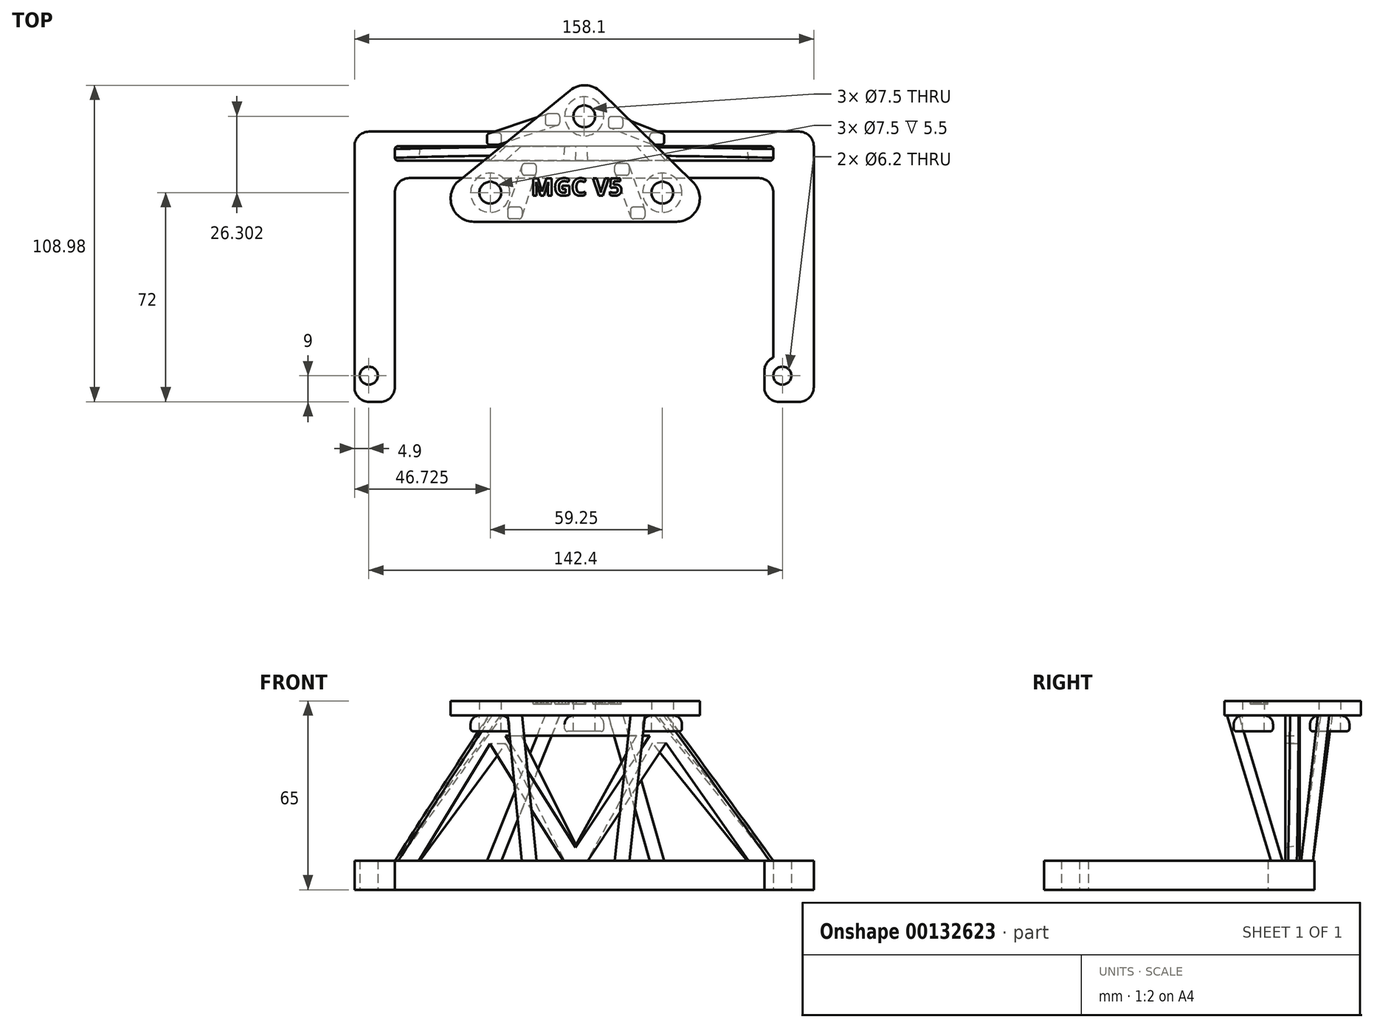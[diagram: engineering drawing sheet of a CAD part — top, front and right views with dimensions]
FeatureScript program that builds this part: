
annotation { "Feature Type Name" : "Feature", "Feature Type Description" : "" }
export const myFeature = defineFeature(function(context is Context, id is Id, definition is map)
    precondition{}
    {
        {
            var Q0;
            Q0=qCreatedBy(makeId("Top.planeOp"),FACE);
            var sketch = newSketch(context, id + "F0", { "sketchPlane" : qUnion([Q0])});
            skCircle(sketch, "E0", {"center": v(71.2, -68) * mm, "radius": 3.1 * mm});
            skCircle(sketch, "E1", {"center": v(-71.2, -68) * mm, "radius": 3.1 * mm});
            skLineSegment(sketch, "E2.bottom", {"start": v(68.1, -61.8) * mm, "end": v(82, -61.8) * mm});
            skLineSegment(sketch, "E2.top", {"start": v(68.1, 0) * mm, "end": v(82, 0) * mm});
            skLineSegment(sketch, "E2.left", {"start": v(68.1, -61.8) * mm, "end": v(68.1, 0) * mm});
            skLineSegment(sketch, "E2.right", {"start": v(82, -61.8) * mm, "end": v(82, 0) * mm});
            skLineSegment(sketch, "E3.bottom", {"start": v(82, -61.8) * mm, "end": v(65, -61.8) * mm});
            skLineSegment(sketch, "E3.top", {"start": v(82, -77) * mm, "end": v(65, -77) * mm});
            skLineSegment(sketch, "E3.left", {"start": v(82, -61.8) * mm, "end": v(82, -77) * mm});
            skLineSegment(sketch, "E3.right", {"start": v(65, -61.8) * mm, "end": v(65, -77) * mm});
            skLineSegment(sketch, "E4.bottom", {"start": v(-76.1, -77) * mm, "end": v(-62.2, -77) * mm});
            skLineSegment(sketch, "E4.top", {"start": v(-76.1, 0) * mm, "end": v(-62.2, 0) * mm});
            skLineSegment(sketch, "E4.left", {"start": v(-76.1, -77) * mm, "end": v(-76.1, 0) * mm});
            skLineSegment(sketch, "E4.right", {"start": v(-62.2, -77) * mm, "end": v(-62.2, 0) * mm});
            skLineSegment(sketch, "E5.bottom", {"start": v(-76.1, 0) * mm, "end": v(82, 0) * mm});
            skLineSegment(sketch, "E5.top", {"start": v(-76.1, 16) * mm, "end": v(82, 16) * mm});
            skLineSegment(sketch, "E5.left", {"start": v(-76.1, 0) * mm, "end": v(-76.1, 16) * mm});
            skLineSegment(sketch, "E5.right", {"start": v(82, 0) * mm, "end": v(82, 16) * mm});
            skPoint(sketch, "E6", {"position": v(68.1, -68) * mm});
            skSolve(sketch);
        }
        {
            var Q0;
            Q0=makeQuery(id+"F0.imprint","IMPRINT",FACE,{"disambiguationData":[TD([[makeQuery(id+"F0.imprint","IMPRINT",EDGE,{"derivedFrom":sQuery(id+"F0.wireOp",EDGE,"E1")}),-1.0]])]});
            var Q1;
            Q1=makeQuery(id+"F0.imprint","IMPRINT",FACE,{"disambiguationData":[TD([[makeQuery(id+"F0.imprint","IMPRINT",EDGE,{"derivedFrom":sQuery(id+"F0.wireOp",EDGE,"E0")}),-1.0]])]});
            var Q2;
            {var subQ0=sQuery(id+"F0.wireOp",EDGE,"E2.left");Q2=makeQuery(id+"F0.imprint","IMPRINT",FACE,{"disambiguationData":[TD([[makeQuery(id+"F0.imprint","IMPRINT",EDGE,{"derivedFrom":subQ0}),-1.0]])]});}
            var Q3;
            Q3=makeQuery(id+"F0.imprint","IMPRINT",FACE,{"disambiguationData":[TD([[makeQuery(id+"F0.imprint","IMPRINT",EDGE,{"derivedFrom":sQuery(id+"F0.wireOp",EDGE,"E5.top")}),-1.0]])]});
            extrude(context, id + "F1", {"entities" : qUnion([Q0, Q1, Q2, Q3]), "depth" : 10 * mm, "symmetric" : true});
        }
        {
            var Q0;
            Q0=qCreatedBy(makeId("Top.planeOp"),FACE);
            cPlane(context, id + "F2", {"entities" : qUnion([Q0]), "cplaneType" : CPlaneType.OFFSET, "offset" : 55 * mm, "width" : 150 * mm, "height" : 150 * mm});
        }
        {
            var Q0;
            Q0=qCreatedBy(id+"F2.planeOp",FACE);
            var sketch = newSketch(context, id + "F3", { "sketchPlane" : qUnion([Q0])});
            skCircle(sketch, "E7", {"center": v(-29.38, -5) * mm, "radius": 3.75 * mm});
            skCircle(sketch, "E8", {"center": v(29.88, -5) * mm, "radius": 3.75 * mm});
            skCircle(sketch, "E9", {"center": v(3, 21.3) * mm, "radius": 3.75 * mm});
            skLineSegment(sketch, "E10", {"start": v(-29.38, -5) * mm, "end": v(3, 21.3) * mm});
            skLineSegment(sketch, "E11", {"start": v(3, 21.3) * mm, "end": v(29.88, -5) * mm});
            skLineSegment(sketch, "E12", {"start": v(29.88, -5) * mm, "end": v(-29.38, -5) * mm});
            skLineSegment(sketch, "E13.0", {"start": v(-40.05, -0.8) * mm, "end": v(-1.92, 30.19) * mm});
            skLineSegment(sketch, "E13.1", {"start": v(34.78, -15) * mm, "end": v(-35, -15) * mm});
            skLineSegment(sketch, "E13.2", {"start": v(8.72, 29.7) * mm, "end": v(40.37, -1.28) * mm});
            skPoint(sketch, "E14.visualSharp", {"position": v(3.62, 34.69) * mm});
            skArc(sketch, "E14.filletArc", {"start": v(8.72, 29.7) * mm, "mid": v(3.49, 31.97) * mm, "end": v(-1.92, 30.19) * mm});
            skPoint(sketch, "E15.visualSharp", {"position": v(-57.54, -15) * mm});
            skArc(sketch, "E15.filletArc", {"start": v(-40.05, -0.8) * mm, "mid": v(-42.55, -9.68) * mm, "end": v(-35, -15) * mm});
            skPoint(sketch, "E16.visualSharp", {"position": v(54.4, -15) * mm});
            skArc(sketch, "E16.filletArc", {"start": v(34.78, -15) * mm, "mid": v(42.19, -10.02) * mm, "end": v(40.37, -1.28) * mm});
            skPoint(sketch, "E17", {"position": v(-0.11, -15) * mm});
            skCircle(sketch, "E18", {"center": v(-0.11, -10) * mm, "radius": 2.5 * mm});
            skSolve(sketch);
        }
        {
            var Q0;
            Q0=makeQuery(id+"F3.imprint","IMPRINT",FACE,{"disambiguationData":[TD([[makeQuery(id+"F3.imprint","IMPRINT",EDGE,{"derivedFrom":sQuery(id+"F3.wireOp",EDGE,"E13.0")}),-1.0]])]});
            var Q1;
            {var subQ0=sQuery(id+"F3.wireOp",EDGE,"E10");var subQ1=sQuery(id+"F3.wireOp",EDGE,"E7");var subQ2=makeQuery(id+"F3.imprint","INTERSECT",VERTEX,{"derivedFrom":[subQ1,subQ0]});Q1=makeQuery(id+"F3.imprint","IMPRINT",FACE,{"disambiguationData":[TD([[makeQuery(id+"F3.imprint","IMPRINT",EDGE,{"disambiguationData":[TD([[subQ2,1.0]])],"derivedFrom":subQ1}),-1.0]])]});}
            var Q2;
            Q2=makeQuery(id+"F3.imprint","IMPRINT",FACE,{"disambiguationData":[TD([[makeQuery(id+"F3.imprint","IMPRINT",EDGE,{"derivedFrom":sQuery(id+"F3.wireOp",EDGE,"E18")}),1.0]])]});
            extrude(context, id + "F4", {"entities" : qUnion([Q0, Q1, Q2]), "depth" : 5 * mm});
        }
        {
            var Q0;
            Q0=makeQuery(id+"F1.opExtrude","SWEPT_FACE",FACE,{"disambiguationData":[OSD([sQuery(id+"F0.wireOp",EDGE,"E5.bottom")])]});
            cPlane(context, id + "F5", {"entities" : qUnion([Q0]), "cplaneType" : CPlaneType.OFFSET, "offset" : 6 * mm, "oppositeDirection" : true, "width" : 150 * mm, "height" : 150 * mm});
        }
        {
            var Q0;
            Q0=qCreatedBy(id+"F5.planeOp",FACE);
            var sketch = newSketch(context, id + "F6", { "sketchPlane" : qUnion([Q0])});
            skLineSegment(sketch, "E19", {"start": v(32.93, 55) * mm, "end": v(-31.7, 55) * mm});
            skLineSegment(sketch, "E20", {"start": v(-31.7, 55) * mm, "end": v(-62.2, 5) * mm});
            skLineSegment(sketch, "E21", {"start": v(-62.2, 5) * mm, "end": v(68.1, 5) * mm});
            skLineSegment(sketch, "E22", {"start": v(68.1, 5) * mm, "end": v(32.93, 55) * mm});
            skSolve(sketch);
        }
        {
            var Q0;
            Q0=makeQuery(id+"F6.imprint","IMPRINT",FACE,{"disambiguationData":[TD([[makeQuery(id+"F6.imprint","IMPRINT",EDGE,{"derivedFrom":sQuery(id+"F6.wireOp",EDGE,"E19")}),1.0]])]});
            cPlane(context, id + "F7", {"entities" : qUnion([Q0]), "cplaneType" : CPlaneType.OFFSET, "offset" : 5 * mm, "oppositeDirection" : true, "width" : 150 * mm, "height" : 150 * mm});
        }
        {
            var Q0;
            Q0=qCreatedBy(id+"F7.planeOp",FACE);
            var sketch = newSketch(context, id + "F8", { "sketchPlane" : qUnion([Q0])});
            skLineSegment(sketch, "E23", {"start": v(27.82, 55) * mm, "end": v(-25.54, 55) * mm});
            skLineSegment(sketch, "E24", {"start": v(68.1, 5) * mm, "end": v(-62.2, 5) * mm});
            skPoint(sketch, "E25.0", {"position": v(68.1, 5) * mm});
            skPoint(sketch, "E26.0", {"position": v(-62.2, 5) * mm});
            skLineSegment(sketch, "E27", {"start": v(27.82, 55) * mm, "end": v(68.1, 5) * mm});
            skLineSegment(sketch, "E28", {"start": v(-25.54, 55) * mm, "end": v(-62.2, 5) * mm});
            skSolve(sketch);
        }
        {
            var Q0;
            Q0=makeQuery(id+"F6.imprint","IMPRINT",FACE,{"disambiguationData":[TD([[makeQuery(id+"F6.imprint","IMPRINT",EDGE,{"derivedFrom":sQuery(id+"F6.wireOp",EDGE,"E19")}),1.0]])]});
            var Q1;
            Q1=makeQuery(id+"F8.imprint","IMPRINT",FACE,{"disambiguationData":[TD([[makeQuery(id+"F8.imprint","IMPRINT",EDGE,{"derivedFrom":sQuery(id+"F8.wireOp",EDGE,"E23")}),1.0]])]});
            loft(context, id + "F9", {"sheetProfilesArray" : [{ "sheetProfileEntities" : qUnion([Q0]) }, { "sheetProfileEntities" : qUnion([Q1]) }]});
        }
        {
            var Q0;
            Q0=makeQuery(id+"F1.opExtrude","SWEPT_EDGE",EDGE,{"disambiguationData":[OSD([sQuery(id+"F0.wireOp",EDGE,"E5.top"),sQuery(id+"F0.wireOp",EDGE,"E5.right")])]});
            var Q1;
            Q1=makeQuery(id+"F1.opExtrude","SWEPT_EDGE",EDGE,{"disambiguationData":[OSD([sQuery(id+"F0.wireOp",EDGE,"E5.top"),sQuery(id+"F0.wireOp",EDGE,"E5.left")])]});
            var Q2;
            Q2=makeQuery(id+"F1.opExtrude","SWEPT_EDGE",EDGE,{"disambiguationData":[OSD([sQuery(id+"F0.wireOp",EDGE,"E4.bottom"),sQuery(id+"F0.wireOp",EDGE,"E4.left")])]});
            var Q3;
            Q3=makeQuery(id+"F1.opExtrude","SWEPT_EDGE",EDGE,{"disambiguationData":[OSD([sQuery(id+"F0.wireOp",EDGE,"E4.bottom"),sQuery(id+"F0.wireOp",EDGE,"E4.right")])]});
            var Q4;
            Q4=makeQuery(id+"F1.opExtrude","SWEPT_EDGE",EDGE,{"disambiguationData":[OSD([sQuery(id+"F0.wireOp",EDGE,"E3.bottom"),sQuery(id+"F0.wireOp",EDGE,"E3.right")])]});
            var Q5;
            Q5=makeQuery(id+"F1.opExtrude","SWEPT_EDGE",EDGE,{"disambiguationData":[OSD([sQuery(id+"F0.wireOp",EDGE,"E3.top"),sQuery(id+"F0.wireOp",EDGE,"E3.right")])]});
            var Q6;
            Q6=makeQuery(id+"F1.opExtrude","SWEPT_EDGE",EDGE,{"disambiguationData":[OSD([sQuery(id+"F0.wireOp",EDGE,"E3.top"),sQuery(id+"F0.wireOp",EDGE,"E3.left")])]});
            var Q7;
            Q7=makeQuery(id+"F1.opExtrude","SWEPT_EDGE",EDGE,{"disambiguationData":[OSD([sQuery(id+"F0.wireOp",EDGE,"E4.right"),sQuery(id+"F0.wireOp",EDGE,"E5.bottom")])]});
            var Q8;
            Q8=makeQuery(id+"F1.opExtrude","SWEPT_EDGE",EDGE,{"disambiguationData":[OSD([sQuery(id+"F0.wireOp",EDGE,"E2.left"),sQuery(id+"F0.wireOp",EDGE,"E5.bottom")])]});
            var Q9;
            Q9=makeQuery(id+"FIhUJoxLiTrV3G5_2.opExtrude","SWEPT_EDGE",EDGE,{"disambiguationData":[OSD([sQuery(id+"F6.wireOp",EDGE,"E19"),sQuery(id+"F6.wireOp",EDGE,"E22")])]});
            var Q10;
            Q10=makeQuery(id+"FIhUJoxLiTrV3G5_2.opExtrude","SWEPT_EDGE",EDGE,{"disambiguationData":[OSD([sQuery(id+"F6.wireOp",EDGE,"E19"),sQuery(id+"F6.wireOp",EDGE,"E20")])]});
            fillet(context, id + "F10", {"entities" : qUnion([Q0, Q1, Q2, Q3, Q4, Q5, Q6, Q7, Q8, Q9, Q10]), "radius" : 5 * mm, "tangentPropagation" : true, "allowEdgeOverflow" : false});
        }
        {
            var Q0;
            Q0=makeQuery(id+"F4.opExtrude","CAP_FACE",FACE,{"disambiguationData":[OSD([sQuery(id+"F3.wireOp",EDGE,"E7"),sQuery(id+"F3.wireOp",EDGE,"E8"),sQuery(id+"F3.wireOp",EDGE,"E9"),sQuery(id+"F3.wireOp",EDGE,"E13.0"),sQuery(id+"F3.wireOp",EDGE,"E13.1"),sQuery(id+"F3.wireOp",EDGE,"E13.2"),sQuery(id+"F3.wireOp",EDGE,"E14.filletArc"),sQuery(id+"F3.wireOp",EDGE,"E15.filletArc"),sQuery(id+"F3.wireOp",EDGE,"E16.filletArc")])],"isStart":false});
            var sketch = newSketch(context, id + "F11", { "sketchPlane" : qUnion([Q0])});
            skText(sketch, "E29", { "text": "MGC V5", "fontName": "OpenSans-Bold.ttf"});
            const initialGuessF11  = {"E29": [-0.01538, -0.006, 1, 0, 0.006]};
            skSetInitialGuess(sketch, initialGuessF11);
            skSolve(sketch);
        }
        {
            var Q0;
            Q0 = qSketchRegion(id + "F11", true);
            extrude(context, id + "F12", {"entities" : qUnion([Q0]), "operationType" : NewBodyOperationType.REMOVE, "oppositeDirection" : true, "depth" : 1 * mm});
        }
        {
            var Q0;
            Q0=makeQuery(id+"F4.opExtrude","SWEPT_BODY",BODY,{"disambiguationData":[OSD([sQuery(id+"F3.wireOp",EDGE,"E7"),sQuery(id+"F3.wireOp",EDGE,"E8"),sQuery(id+"F3.wireOp",EDGE,"E9"),sQuery(id+"F3.wireOp",EDGE,"E13.0"),sQuery(id+"F3.wireOp",EDGE,"E13.1"),sQuery(id+"F3.wireOp",EDGE,"E13.2"),sQuery(id+"F3.wireOp",EDGE,"E14.filletArc"),sQuery(id+"F3.wireOp",EDGE,"E15.filletArc"),sQuery(id+"F3.wireOp",EDGE,"E16.filletArc")])]});
            var Q1;
            Q1=makeQuery(id+"F1.opExtrude","SWEPT_BODY",BODY,{"disambiguationData":[OSD([sQuery(id+"F0.wireOp",EDGE,"E0"),sQuery(id+"F0.wireOp",EDGE,"E1"),sQuery(id+"F0.wireOp",EDGE,"E2.left"),sQuery(id+"F0.wireOp",EDGE,"E2.right"),sQuery(id+"F0.wireOp",EDGE,"E3.bottom"),sQuery(id+"F0.wireOp",EDGE,"E3.top"),sQuery(id+"F0.wireOp",EDGE,"E3.left"),sQuery(id+"F0.wireOp",EDGE,"E3.right"),sQuery(id+"F0.wireOp",EDGE,"E4.bottom"),sQuery(id+"F0.wireOp",EDGE,"E4.left"),sQuery(id+"F0.wireOp",EDGE,"E4.right"),sQuery(id+"F0.wireOp",EDGE,"E5.bottom"),sQuery(id+"F0.wireOp",EDGE,"E5.top"),sQuery(id+"F0.wireOp",EDGE,"E5.left"),sQuery(id+"F0.wireOp",EDGE,"E5.right")])]});
            var Q2;
            Q2=makeQuery(id+"F9.opLoft","SWEPT_BODY",BODY,{"disambiguationData":[OSD([makeQuery(id+"F6.imprint","IMPRINT",FACE,{"disambiguationData":[TD([[makeQuery(id+"F6.imprint","IMPRINT",EDGE,{"derivedFrom":sQuery(id+"F6.wireOp",EDGE,"E19")}),1.0]])]}),makeQuery(id+"F8.imprint","IMPRINT",FACE,{"disambiguationData":[TD([[makeQuery(id+"F8.imprint","IMPRINT",EDGE,{"derivedFrom":sQuery(id+"F8.wireOp",EDGE,"E23")}),1.0]])]})])]});
            booleanBodies(context, id + "F13", {"operationType" : BooleanOperationType.UNION, "tools" : qUnion([Q0, Q1, Q2])});
        }
        {
            var Q0;
            Q0=makeQuery(id+"F1.opExtrude","CAP_FACE",FACE,{"disambiguationData":[OSD([sQuery(id+"F0.wireOp",EDGE,"E0"),sQuery(id+"F0.wireOp",EDGE,"E1"),sQuery(id+"F0.wireOp",EDGE,"E2.left"),sQuery(id+"F0.wireOp",EDGE,"E2.right"),sQuery(id+"F0.wireOp",EDGE,"E3.bottom"),sQuery(id+"F0.wireOp",EDGE,"E3.top"),sQuery(id+"F0.wireOp",EDGE,"E3.left"),sQuery(id+"F0.wireOp",EDGE,"E3.right"),sQuery(id+"F0.wireOp",EDGE,"E4.bottom"),sQuery(id+"F0.wireOp",EDGE,"E4.left"),sQuery(id+"F0.wireOp",EDGE,"E4.right"),sQuery(id+"F0.wireOp",EDGE,"E5.bottom"),sQuery(id+"F0.wireOp",EDGE,"E5.top"),sQuery(id+"F0.wireOp",EDGE,"E5.left"),sQuery(id+"F0.wireOp",EDGE,"E5.right")])],"isStart":false});
            var sketch = newSketch(context, id + "F14", { "sketchPlane" : qUnion([Q0])});
            skLineSegment(sketch, "E30.bottom", {"start": v(-13.5, 1) * mm, "end": v(-18.5, 1) * mm});
            skLineSegment(sketch, "E30.top", {"start": v(-13.5, 5) * mm, "end": v(-18.5, 5) * mm});
            skLineSegment(sketch, "E30.left", {"start": v(-13.5, 1) * mm, "end": v(-13.5, 5) * mm});
            skLineSegment(sketch, "E30.right", {"start": v(-18.5, 1) * mm, "end": v(-18.5, 5) * mm});
            skPoint(sketch, "E30.middle", {"position": v(-16, 3) * mm});
            skLineSegment(sketch, "E31.bottom", {"start": v(18.5, 1) * mm, "end": v(13.5, 1) * mm});
            skLineSegment(sketch, "E31.top", {"start": v(18.5, 5) * mm, "end": v(13.5, 5) * mm});
            skLineSegment(sketch, "E31.left", {"start": v(18.5, 1) * mm, "end": v(18.5, 5) * mm});
            skLineSegment(sketch, "E31.right", {"start": v(13.5, 1) * mm, "end": v(13.5, 5) * mm});
            skPoint(sketch, "E31.middle", {"position": v(16, 3) * mm});
            skLineSegment(sketch, "E32.bottom", {"start": v(-25.5, 11.5) * mm, "end": v(-30.5, 11.5) * mm});
            skLineSegment(sketch, "E32.top", {"start": v(-25.5, 15.5) * mm, "end": v(-30.5, 15.5) * mm});
            skLineSegment(sketch, "E32.left", {"start": v(-25.5, 11.5) * mm, "end": v(-25.5, 15.5) * mm});
            skLineSegment(sketch, "E32.right", {"start": v(-30.5, 11.5) * mm, "end": v(-30.5, 15.5) * mm});
            skPoint(sketch, "E32.middle", {"position": v(-28, 13.5) * mm});
            skLineSegment(sketch, "E33.bottom", {"start": v(30.5, 11.5) * mm, "end": v(25.5, 11.5) * mm});
            skLineSegment(sketch, "E33.top", {"start": v(30.5, 15.5) * mm, "end": v(25.5, 15.5) * mm});
            skLineSegment(sketch, "E33.left", {"start": v(30.5, 11.5) * mm, "end": v(30.5, 15.5) * mm});
            skLineSegment(sketch, "E33.right", {"start": v(25.5, 11.5) * mm, "end": v(25.5, 15.5) * mm});
            skPoint(sketch, "E33.middle", {"position": v(28, 13.5) * mm});
            skSolve(sketch);
        }
        {
            var Q0;
            Q0=qCreatedBy(id+"F2.planeOp",FACE);
            var sketch = newSketch(context, id + "F15", { "sketchPlane" : qUnion([Q0])});
            skCircle(sketch, "E34.0", {"center": v(3, 21.3) * mm, "radius": 6.75 * mm});
            skCircle(sketch, "E35.0", {"center": v(-29.38, -5) * mm, "radius": 3.75 * mm});
            skCircle(sketch, "E36.0", {"center": v(29.88, -5) * mm, "radius": 3.75 * mm});
            skCircle(sketch, "E37.0", {"center": v(3, 21.3) * mm, "radius": 3.75 * mm});
            skCircle(sketch, "E38.0", {"center": v(-29.38, -5) * mm, "radius": 6.75 * mm});
            skCircle(sketch, "E39.0", {"center": v(29.88, -5) * mm, "radius": 6.75 * mm});
            skLineSegment(sketch, "E40.bottom", {"start": v(-18.39, -10) * mm, "end": v(-23.39, -10) * mm});
            skLineSegment(sketch, "E40.top", {"start": v(-18.39, -14) * mm, "end": v(-23.39, -14) * mm});
            skLineSegment(sketch, "E40.left", {"start": v(-18.39, -10) * mm, "end": v(-18.39, -14) * mm});
            skLineSegment(sketch, "E40.right", {"start": v(-23.39, -10) * mm, "end": v(-23.39, -14) * mm});
            skPoint(sketch, "E40.middle", {"position": v(-20.89, -12) * mm});
            skLineSegment(sketch, "E41.bottom", {"start": v(23.89, -10) * mm, "end": v(18.89, -10) * mm});
            skLineSegment(sketch, "E41.top", {"start": v(23.89, -14) * mm, "end": v(18.89, -14) * mm});
            skLineSegment(sketch, "E41.left", {"start": v(23.89, -10) * mm, "end": v(23.89, -14) * mm});
            skLineSegment(sketch, "E41.right", {"start": v(18.89, -10) * mm, "end": v(18.89, -14) * mm});
            skPoint(sketch, "E41.middle", {"position": v(21.39, -12) * mm});
            skLineSegment(sketch, "E42.bottom", {"start": v(16.28, 21.14) * mm, "end": v(11.28, 21.14) * mm});
            skLineSegment(sketch, "E42.top", {"start": v(16.28, 17.14) * mm, "end": v(11.28, 17.14) * mm});
            skLineSegment(sketch, "E42.left", {"start": v(16.28, 21.14) * mm, "end": v(16.28, 17.14) * mm});
            skLineSegment(sketch, "E42.right", {"start": v(11.28, 21.14) * mm, "end": v(11.28, 17.14) * mm});
            skPoint(sketch, "E42.middle", {"position": v(13.78, 19.14) * mm});
            skLineSegment(sketch, "E43.bottom", {"start": v(-5.44, 22.14) * mm, "end": v(-10.44, 22.14) * mm});
            skLineSegment(sketch, "E43.top", {"start": v(-5.44, 18.14) * mm, "end": v(-10.44, 18.14) * mm});
            skLineSegment(sketch, "E43.left", {"start": v(-5.44, 22.14) * mm, "end": v(-5.44, 18.14) * mm});
            skLineSegment(sketch, "E43.right", {"start": v(-10.44, 22.14) * mm, "end": v(-10.44, 18.14) * mm});
            skPoint(sketch, "E43.middle", {"position": v(-7.94, 20.14) * mm});
            skSolve(sketch);
        }
        {
            var Q0;
            Q0=makeQuery(id+"F15.imprint","IMPRINT",FACE,{"disambiguationData":[TD([[makeQuery(id+"F15.imprint","IMPRINT",EDGE,{"derivedFrom":sQuery(id+"F15.wireOp",EDGE,"E35.0")}),-1.0]])]});
            var Q1;
            Q1=makeQuery(id+"F15.imprint","IMPRINT",FACE,{"disambiguationData":[TD([[makeQuery(id+"F15.imprint","IMPRINT",EDGE,{"derivedFrom":sQuery(id+"F15.wireOp",EDGE,"E36.0")}),-1.0]])]});
            var Q2;
            Q2=makeQuery(id+"F15.imprint","IMPRINT",FACE,{"disambiguationData":[TD([[makeQuery(id+"F15.imprint","IMPRINT",EDGE,{"derivedFrom":sQuery(id+"F15.wireOp",EDGE,"E34.0")}),1.0]])]});
            extrude(context, id + "F16", {"entities" : qUnion([Q0, Q1, Q2]), "oppositeDirection" : true, "depth" : 5.5 * mm});
        }
        {
            var Q0;
            Q0=makeQuery(id+"F16.opExtrude","CAP_EDGE",EDGE,{"disambiguationData":[OSD([sQuery(id+"F15.wireOp",EDGE,"94168fc8-b406-4e30-aa3f-1900fabe6d56.0")])],"isStart":false});
            var Q1;
            Q1=makeQuery(id+"F16.opExtrude","CAP_EDGE",EDGE,{"disambiguationData":[OSD([sQuery(id+"F15.wireOp",EDGE,"0267a17e-6969-43b7-bb86-29099e7b7c24.0")])],"isStart":false});
            var Q2;
            Q2=makeQuery(id+"F16.opExtrude","CAP_EDGE",EDGE,{"disambiguationData":[OSD([sQuery(id+"F15.wireOp",EDGE,"E34.0")])],"isStart":false});
            var Q3;
            Q3=makeQuery(id+"F16.opExtrude","CAP_EDGE",EDGE,{"disambiguationData":[OSD([sQuery(id+"F15.wireOp",EDGE,"E38.0")])],"isStart":false});
            var Q4;
            Q4=makeQuery(id+"F16.opExtrude","CAP_EDGE",EDGE,{"disambiguationData":[OSD([sQuery(id+"F15.wireOp",EDGE,"E39.0")])],"isStart":false});
            fillet(context, id + "F17", {"entities" : qUnion([Q0, Q1, Q2, Q3, Q4]), "radius" : 1 * mm, "tangentPropagation" : true, "allowEdgeOverflow" : false});
        }
        {
            var Q0;
            Q0=makeQuery(id+"F9.opLoft","CAP_FACE",FACE,{"disambiguationData":[OSD([makeQuery(id+"F6.imprint","IMPRINT",FACE,{"disambiguationData":[TD([[makeQuery(id+"F6.imprint","IMPRINT",EDGE,{"derivedFrom":sQuery(id+"F6.wireOp",EDGE,"E19")}),1.0]])]})])],"isStart":true});
            var sketch = newSketch(context, id + "F18", { "sketchPlane" : qUnion([Q0])});
            skLineSegment(sketch, "E44", {"start": v(0, 4) * mm, "end": v(-55.78, 4) * mm});
            skLineSegment(sketch, "E45", {"start": v(-55.78, 4) * mm, "end": v(-28.33, 49) * mm});
            skLineSegment(sketch, "E46", {"start": v(-28.33, 49) * mm, "end": v(0, 4) * mm});
            skLineSegment(sketch, "E47", {"start": v(0, 4) * mm, "end": v(61.47, 4) * mm});
            skLineSegment(sketch, "E48", {"start": v(61.47, 4) * mm, "end": v(29.82, 49) * mm});
            skLineSegment(sketch, "E49", {"start": v(29.82, 49) * mm, "end": v(0, 4) * mm});
            skLineSegment(sketch, "E50", {"start": v(-28.33, 49) * mm, "end": v(29.82, 49) * mm});
            skLineSegment(sketch, "E51.0", {"start": v(-54, 5) * mm, "end": v(-29.48, 45.2) * mm});
            skLineSegment(sketch, "E51.1", {"start": v(-4.17, 5) * mm, "end": v(-54, 5) * mm});
            skLineSegment(sketch, "E51.2", {"start": v(-29.48, 45.2) * mm, "end": v(-4.17, 5) * mm});
            skLineSegment(sketch, "E52.0", {"start": v(-24.15, 48) * mm, "end": v(25.56, 48) * mm});
            skLineSegment(sketch, "E52.1", {"start": v(-24.15, 48) * mm, "end": v(0.06, 9.53) * mm});
            skLineSegment(sketch, "E52.2", {"start": v(25.56, 48) * mm, "end": v(0.06, 9.53) * mm});
            skLineSegment(sketch, "E53.0", {"start": v(4.26, 5) * mm, "end": v(59.54, 5) * mm});
            skLineSegment(sketch, "E53.1", {"start": v(31.08, 45.47) * mm, "end": v(4.26, 5) * mm});
            skLineSegment(sketch, "E53.2", {"start": v(59.54, 5) * mm, "end": v(31.08, 45.47) * mm});
            skSolve(sketch);
        }
        {
            var Q0;
            Q0=makeQuery(id+"F9.opLoft","CAP_FACE",FACE,{"disambiguationData":[OSD([makeQuery(id+"F8.imprint","IMPRINT",FACE,{"disambiguationData":[TD([[makeQuery(id+"F8.imprint","IMPRINT",EDGE,{"derivedFrom":sQuery(id+"F8.wireOp",EDGE,"E23")}),1.0]])]})])],"isStart":true});
            var sketch = newSketch(context, id + "F19", { "sketchPlane" : qUnion([Q0])});
            skLineSegment(sketch, "E54", {"start": v(0, 4) * mm, "end": v(-61.2, 4) * mm});
            skLineSegment(sketch, "E55", {"start": v(-61.2, 4) * mm, "end": v(-24.95, 49) * mm});
            skLineSegment(sketch, "E56", {"start": v(-24.95, 49) * mm, "end": v(0, 4) * mm});
            skLineSegment(sketch, "E57", {"start": v(0, 4) * mm, "end": v(55.5, 4) * mm});
            skLineSegment(sketch, "E58", {"start": v(55.5, 4) * mm, "end": v(22.5, 49) * mm});
            skLineSegment(sketch, "E59", {"start": v(22.5, 49) * mm, "end": v(0, 4) * mm});
            skLineSegment(sketch, "E60", {"start": v(-24.95, 49) * mm, "end": v(22.5, 49) * mm});
            skLineSegment(sketch, "E61.0", {"start": v(-59.11, 5) * mm, "end": v(-26.46, 45.53) * mm});
            skLineSegment(sketch, "E61.1", {"start": v(-3.98, 5) * mm, "end": v(-59.11, 5) * mm});
            skLineSegment(sketch, "E61.2", {"start": v(-26.46, 45.53) * mm, "end": v(-3.98, 5) * mm});
            skLineSegment(sketch, "E62.0", {"start": v(-20.97, 48) * mm, "end": v(18.65, 48) * mm});
            skLineSegment(sketch, "E62.1", {"start": v(-20.97, 48) * mm, "end": v(-0.14, 10.43) * mm});
            skLineSegment(sketch, "E62.2", {"start": v(18.65, 48) * mm, "end": v(-0.14, 10.43) * mm});
            skLineSegment(sketch, "E63.0", {"start": v(3.85, 5) * mm, "end": v(53.52, 5) * mm});
            skLineSegment(sketch, "E63.1", {"start": v(24, 45.27) * mm, "end": v(3.85, 5) * mm});
            skLineSegment(sketch, "E63.2", {"start": v(53.52, 5) * mm, "end": v(24, 45.27) * mm});
            skSolve(sketch);
        }
        {
            var Q1;
            Q1=makeQuery(id+"F18.imprint","IMPRINT",FACE,{"disambiguationData":[TD([[makeQuery(id+"F18.imprint","IMPRINT",EDGE,{"derivedFrom":sQuery(id+"F18.wireOp",EDGE,"E52.0")}),-1.0]])]});
            var Q2;
            Q2=makeQuery(id+"F19.imprint","IMPRINT",FACE,{"disambiguationData":[TD([[makeQuery(id+"F19.imprint","IMPRINT",EDGE,{"derivedFrom":sQuery(id+"F19.wireOp",EDGE,"E62.0")}),-1.0]])]});
            loft(context, id + "F20", {"operationType" : NewBodyOperationType.REMOVE, "sheetProfilesArray" : [{ "sheetProfileEntities" : qUnion([Q1]) }, { "sheetProfileEntities" : qUnion([Q2]) }]});
        }
        {
            var Q1;
            Q1=makeQuery(id+"F18.imprint","IMPRINT",FACE,{"disambiguationData":[TD([[makeQuery(id+"F18.imprint","IMPRINT",EDGE,{"derivedFrom":sQuery(id+"F18.wireOp",EDGE,"E53.0")}),-1.0]])]});
            var Q2;
            Q2=makeQuery(id+"F19.imprint","IMPRINT",FACE,{"disambiguationData":[TD([[makeQuery(id+"F19.imprint","IMPRINT",EDGE,{"derivedFrom":sQuery(id+"F19.wireOp",EDGE,"E61.0")}),-1.0]])]});
            loft(context, id + "F21", {"operationType" : NewBodyOperationType.REMOVE, "sheetProfilesArray" : [{ "sheetProfileEntities" : qUnion([Q1]) }, { "sheetProfileEntities" : qUnion([Q2]) }]});
        }
        {
            var Q1;
            Q1=makeQuery(id+"F19.imprint","IMPRINT",FACE,{"disambiguationData":[TD([[makeQuery(id+"F19.imprint","IMPRINT",EDGE,{"derivedFrom":sQuery(id+"F19.wireOp",EDGE,"E63.0")}),1.0]])]});
            var Q2;
            Q2=makeQuery(id+"F18.imprint","IMPRINT",FACE,{"disambiguationData":[TD([[makeQuery(id+"F18.imprint","IMPRINT",EDGE,{"derivedFrom":sQuery(id+"F18.wireOp",EDGE,"E51.0")}),-1.0]])]});
            loft(context, id + "F22", {"operationType" : NewBodyOperationType.REMOVE, "sheetProfilesArray" : [{ "sheetProfileEntities" : qUnion([Q1]) }, { "sheetProfileEntities" : qUnion([Q2]) }]});
        }
        {
            var Q1;
            Q1=makeQuery(id+"F15.imprint","IMPRINT",FACE,{"disambiguationData":[TD([[makeQuery(id+"F15.imprint","IMPRINT",EDGE,{"derivedFrom":sQuery(id+"F15.wireOp",EDGE,"E43.bottom")}),1.0]])]});
            var Q2;
            Q2=makeQuery(id+"F14.imprint","IMPRINT",FACE,{"disambiguationData":[TD([[makeQuery(id+"F14.imprint","IMPRINT",EDGE,{"derivedFrom":sQuery(id+"F14.wireOp",EDGE,"E32.bottom")}),-1.0]])]});
            loft(context, id + "F23", {"operationType" : NewBodyOperationType.ADD, "sheetProfilesArray" : [{ "sheetProfileEntities" : qUnion([Q1]) }, { "sheetProfileEntities" : qUnion([Q2]) }]});
        }
        {
            var Q1;
            Q1=makeQuery(id+"F15.imprint","IMPRINT",FACE,{"disambiguationData":[TD([[makeQuery(id+"F15.imprint","IMPRINT",EDGE,{"derivedFrom":sQuery(id+"F15.wireOp",EDGE,"E42.bottom")}),1.0]])]});
            var Q2;
            Q2=makeQuery(id+"F14.imprint","IMPRINT",FACE,{"disambiguationData":[TD([[makeQuery(id+"F14.imprint","IMPRINT",EDGE,{"derivedFrom":sQuery(id+"F14.wireOp",EDGE,"E33.bottom")}),-1.0]])]});
            loft(context, id + "F24", {"operationType" : NewBodyOperationType.ADD, "sheetProfilesArray" : [{ "sheetProfileEntities" : qUnion([Q1]) }, { "sheetProfileEntities" : qUnion([Q2]) }]});
        }
        {
            var Q1;
            Q1=makeQuery(id+"F15.imprint","IMPRINT",FACE,{"disambiguationData":[TD([[makeQuery(id+"F15.imprint","IMPRINT",EDGE,{"derivedFrom":sQuery(id+"F15.wireOp",EDGE,"E40.bottom")}),1.0]])]});
            var Q2;
            Q2=makeQuery(id+"F14.imprint","IMPRINT",FACE,{"disambiguationData":[TD([[makeQuery(id+"F14.imprint","IMPRINT",EDGE,{"derivedFrom":sQuery(id+"F14.wireOp",EDGE,"E30.bottom")}),-1.0]])]});
            loft(context, id + "F25", {"operationType" : NewBodyOperationType.ADD, "sheetProfilesArray" : [{ "sheetProfileEntities" : qUnion([Q1]) }, { "sheetProfileEntities" : qUnion([Q2]) }]});
        }
        {
            var Q1;
            Q1=makeQuery(id+"F15.imprint","IMPRINT",FACE,{"disambiguationData":[TD([[makeQuery(id+"F15.imprint","IMPRINT",EDGE,{"derivedFrom":sQuery(id+"F15.wireOp",EDGE,"E41.bottom")}),1.0]])]});
            var Q2;
            Q2=makeQuery(id+"F14.imprint","IMPRINT",FACE,{"disambiguationData":[TD([[makeQuery(id+"F14.imprint","IMPRINT",EDGE,{"derivedFrom":sQuery(id+"F14.wireOp",EDGE,"E31.bottom")}),-1.0]])]});
            loft(context, id + "F26", {"operationType" : NewBodyOperationType.ADD, "sheetProfilesArray" : [{ "sheetProfileEntities" : qUnion([Q1]) }, { "sheetProfileEntities" : qUnion([Q2]) }]});
        }
        {
            var Q0;
            Q0=makeQuery(id+"F9.opLoft","MID_CAP_EDGE",EDGE,{"disambiguationData":[OSD([sQuery(id+"F6.wireOp",EDGE,"E19"),sQuery(id+"F6.wireOp",EDGE,"E20"),sQuery(id+"F6.wireOp",EDGE,"E21")])],"capPos":0.0});
            var Q1;
            Q1=makeQuery(id+"F9.opLoft","MID_CAP_EDGE",EDGE,{"disambiguationData":[OSD([sQuery(id+"F8.wireOp",EDGE,"E23"),sQuery(id+"F8.wireOp",EDGE,"E24"),sQuery(id+"F8.wireOp",EDGE,"E28")])],"capPos":1.0});
            var Q2;
            Q2=makeQuery(id+"F9.opLoft","MID_CAP_EDGE",EDGE,{"disambiguationData":[OSD([sQuery(id+"F8.wireOp",EDGE,"E23"),sQuery(id+"F8.wireOp",EDGE,"E24"),sQuery(id+"F8.wireOp",EDGE,"E27")])],"capPos":1.0});
            var Q3;
            Q3=makeQuery(id+"F9.opLoft","MID_CAP_EDGE",EDGE,{"disambiguationData":[OSD([sQuery(id+"F6.wireOp",EDGE,"E19"),sQuery(id+"F6.wireOp",EDGE,"E21"),sQuery(id+"F6.wireOp",EDGE,"E22")])],"capPos":0.0});
            var Q4;
            {var subQ0=sQuery(id+"F18.wireOp",EDGE,"E51.0");var subQ1=sQuery(id+"F18.wireOp",EDGE,"E51.2");var subQ2=sQuery(id+"F18.wireOp",EDGE,"E51.1");var subQ3=sQuery(id+"F6.wireOp",EDGE,"E22");var subQ4=sQuery(id+"F6.wireOp",EDGE,"E21");var subQ5=sQuery(id+"F6.wireOp",EDGE,"E20");Q4=makeQuery(id+"F22.boolean.opBoolean","COPY",EDGE,{"derivedFrom":makeQuery(id+"F22.opLoft","MID_CAP_EDGE",EDGE,{"disambiguationData":[OSD([subQ5,subQ4,subQ3,subQ0,subQ2,subQ1]),TDD([makeQuery(id+"F18.imprint","INTERSECT",VERTEX,{"derivedFrom":[makeQuery(id+"F9.opLoft","MID_CAP_EDGE",EDGE,{"disambiguationData":[OSD([subQ5,subQ4,subQ3])],"capPos":0.0}),subQ0,subQ2]}),makeQuery(id+"F18.imprint","INTERSECT",VERTEX,{"derivedFrom":[subQ0,subQ1]}),makeQuery(id+"F18.imprint","IMPRINT",EDGE,{"derivedFrom":subQ0})])],"capPos":1.0})});}
            var Q5;
            {var subQ0=sQuery(id+"F19.wireOp",EDGE,"E63.2");var subQ1=sQuery(id+"F19.wireOp",EDGE,"E63.1");var subQ2=sQuery(id+"F19.wireOp",EDGE,"E63.0");var subQ3=sQuery(id+"F8.wireOp",EDGE,"E28");var subQ4=sQuery(id+"F8.wireOp",EDGE,"E27");var subQ5=sQuery(id+"F8.wireOp",EDGE,"E24");Q5=makeQuery(id+"F22.boolean.opBoolean","COPY",EDGE,{"derivedFrom":makeQuery(id+"F22.opLoft","MID_CAP_EDGE",EDGE,{"disambiguationData":[OSD([subQ5,subQ4,subQ3,subQ2,subQ1,subQ0]),TDD([makeQuery(id+"F19.imprint","INTERSECT",VERTEX,{"derivedFrom":[makeQuery(id+"F9.opLoft","MID_CAP_EDGE",EDGE,{"disambiguationData":[OSD([subQ5,subQ4,subQ3])],"capPos":1.0}),subQ2,subQ0]}),makeQuery(id+"F19.imprint","INTERSECT",VERTEX,{"derivedFrom":[subQ1,subQ0]}),makeQuery(id+"F19.imprint","IMPRINT",EDGE,{"derivedFrom":subQ0})])],"capPos":0.0})});}
            var Q6;
            {var subQ0=sQuery(id+"F19.wireOp",EDGE,"E61.0");var subQ1=sQuery(id+"F19.wireOp",EDGE,"E61.2");var subQ2=sQuery(id+"F19.wireOp",EDGE,"E61.1");var subQ3=sQuery(id+"F8.wireOp",EDGE,"E28");var subQ4=sQuery(id+"F8.wireOp",EDGE,"E27");var subQ5=sQuery(id+"F8.wireOp",EDGE,"E24");Q6=makeQuery(id+"F21.boolean.opBoolean","COPY",EDGE,{"derivedFrom":makeQuery(id+"F21.opLoft","MID_CAP_EDGE",EDGE,{"disambiguationData":[OSD([subQ5,subQ4,subQ3,subQ0,subQ2,subQ1]),TDD([makeQuery(id+"F19.imprint","INTERSECT",VERTEX,{"derivedFrom":[makeQuery(id+"F9.opLoft","MID_CAP_EDGE",EDGE,{"disambiguationData":[OSD([subQ5,subQ4,subQ3])],"capPos":1.0}),subQ0,subQ2]}),makeQuery(id+"F19.imprint","INTERSECT",VERTEX,{"derivedFrom":[subQ0,subQ1]}),makeQuery(id+"F19.imprint","IMPRINT",EDGE,{"derivedFrom":subQ0})])],"capPos":1.0})});}
            var Q7;
            {var subQ0=sQuery(id+"F18.wireOp",EDGE,"E53.2");var subQ1=sQuery(id+"F18.wireOp",EDGE,"E53.1");var subQ2=sQuery(id+"F18.wireOp",EDGE,"E53.0");var subQ3=sQuery(id+"F6.wireOp",EDGE,"E22");var subQ4=sQuery(id+"F6.wireOp",EDGE,"E21");var subQ5=sQuery(id+"F6.wireOp",EDGE,"E20");Q7=makeQuery(id+"F21.boolean.opBoolean","COPY",EDGE,{"derivedFrom":makeQuery(id+"F21.opLoft","MID_CAP_EDGE",EDGE,{"disambiguationData":[OSD([subQ5,subQ4,subQ3,subQ2,subQ1,subQ0]),TDD([makeQuery(id+"F18.imprint","INTERSECT",VERTEX,{"derivedFrom":[makeQuery(id+"F9.opLoft","MID_CAP_EDGE",EDGE,{"disambiguationData":[OSD([subQ5,subQ4,subQ3])],"capPos":0.0}),subQ2,subQ0]}),makeQuery(id+"F18.imprint","INTERSECT",VERTEX,{"derivedFrom":[subQ1,subQ0]}),makeQuery(id+"F18.imprint","IMPRINT",EDGE,{"derivedFrom":subQ0})])],"capPos":0.0})});}
            var Q8;
            {var subQ0=sQuery(id+"F18.wireOp",EDGE,"E52.0");var subQ1=sQuery(id+"F18.wireOp",EDGE,"E52.2");var subQ2=sQuery(id+"F18.wireOp",EDGE,"E52.1");Q8=makeQuery(id+"F20.boolean.opBoolean","COPY",EDGE,{"derivedFrom":makeQuery(id+"F20.opLoft","MID_CAP_EDGE",EDGE,{"disambiguationData":[OSD([subQ0,subQ2,subQ1]),TDD([makeQuery(id+"F18.imprint","INTERSECT",VERTEX,{"derivedFrom":[subQ0,subQ2]}),makeQuery(id+"F18.imprint","INTERSECT",VERTEX,{"derivedFrom":[subQ0,subQ1]}),makeQuery(id+"F18.imprint","IMPRINT",EDGE,{"derivedFrom":subQ0})])],"capPos":0.0})});}
            var Q9;
            {var subQ0=sQuery(id+"F19.wireOp",EDGE,"E62.0");var subQ1=sQuery(id+"F19.wireOp",EDGE,"E62.2");var subQ2=sQuery(id+"F19.wireOp",EDGE,"E62.1");Q9=makeQuery(id+"F20.boolean.opBoolean","COPY",EDGE,{"derivedFrom":makeQuery(id+"F20.opLoft","MID_CAP_EDGE",EDGE,{"disambiguationData":[OSD([subQ0,subQ2,subQ1]),TDD([makeQuery(id+"F19.imprint","INTERSECT",VERTEX,{"derivedFrom":[subQ0,subQ2]}),makeQuery(id+"F19.imprint","INTERSECT",VERTEX,{"derivedFrom":[subQ0,subQ1]}),makeQuery(id+"F19.imprint","IMPRINT",EDGE,{"derivedFrom":subQ0})])],"capPos":1.0})});}
            var Q10;
            {var subQ0=sQuery(id+"F19.wireOp",EDGE,"E62.1");var subQ1=sQuery(id+"F19.wireOp",EDGE,"E62.2");var subQ2=sQuery(id+"F19.wireOp",EDGE,"E62.0");Q10=makeQuery(id+"F20.boolean.opBoolean","COPY",EDGE,{"derivedFrom":makeQuery(id+"F20.opLoft","MID_CAP_EDGE",EDGE,{"disambiguationData":[OSD([subQ2,subQ0,subQ1]),TDD([makeQuery(id+"F19.imprint","INTERSECT",VERTEX,{"derivedFrom":[subQ2,subQ0]}),makeQuery(id+"F19.imprint","INTERSECT",VERTEX,{"derivedFrom":[subQ0,subQ1]}),makeQuery(id+"F19.imprint","IMPRINT",EDGE,{"derivedFrom":subQ0})])],"capPos":1.0})});}
            var Q11;
            {var subQ0=sQuery(id+"F19.wireOp",EDGE,"E62.2");var subQ1=sQuery(id+"F19.wireOp",EDGE,"E62.1");var subQ2=sQuery(id+"F19.wireOp",EDGE,"E62.0");Q11=makeQuery(id+"F20.boolean.opBoolean","COPY",EDGE,{"derivedFrom":makeQuery(id+"F20.opLoft","MID_CAP_EDGE",EDGE,{"disambiguationData":[OSD([subQ2,subQ1,subQ0]),TDD([makeQuery(id+"F19.imprint","INTERSECT",VERTEX,{"derivedFrom":[subQ2,subQ0]}),makeQuery(id+"F19.imprint","INTERSECT",VERTEX,{"derivedFrom":[subQ1,subQ0]}),makeQuery(id+"F19.imprint","IMPRINT",EDGE,{"derivedFrom":subQ0})])],"capPos":1.0})});}
            var Q12;
            {var subQ0=sQuery(id+"F18.wireOp",EDGE,"E52.2");var subQ1=sQuery(id+"F18.wireOp",EDGE,"E52.1");var subQ2=sQuery(id+"F18.wireOp",EDGE,"E52.0");Q12=makeQuery(id+"F20.boolean.opBoolean","COPY",EDGE,{"derivedFrom":makeQuery(id+"F20.opLoft","MID_CAP_EDGE",EDGE,{"disambiguationData":[OSD([subQ2,subQ1,subQ0]),TDD([makeQuery(id+"F18.imprint","INTERSECT",VERTEX,{"derivedFrom":[subQ2,subQ0]}),makeQuery(id+"F18.imprint","INTERSECT",VERTEX,{"derivedFrom":[subQ1,subQ0]}),makeQuery(id+"F18.imprint","IMPRINT",EDGE,{"derivedFrom":subQ0})])],"capPos":0.0})});}
            var Q13;
            {var subQ0=sQuery(id+"F18.wireOp",EDGE,"E52.1");var subQ1=sQuery(id+"F18.wireOp",EDGE,"E52.2");var subQ2=sQuery(id+"F18.wireOp",EDGE,"E52.0");Q13=makeQuery(id+"F20.boolean.opBoolean","COPY",EDGE,{"derivedFrom":makeQuery(id+"F20.opLoft","MID_CAP_EDGE",EDGE,{"disambiguationData":[OSD([subQ2,subQ0,subQ1]),TDD([makeQuery(id+"F18.imprint","INTERSECT",VERTEX,{"derivedFrom":[subQ2,subQ0]}),makeQuery(id+"F18.imprint","INTERSECT",VERTEX,{"derivedFrom":[subQ0,subQ1]}),makeQuery(id+"F18.imprint","IMPRINT",EDGE,{"derivedFrom":subQ0})])],"capPos":0.0})});}
            var Q14;
            {var subQ0=sQuery(id+"F18.wireOp",EDGE,"E53.1");var subQ1=sQuery(id+"F18.wireOp",EDGE,"E53.2");var subQ2=sQuery(id+"F18.wireOp",EDGE,"E53.0");var subQ3=sQuery(id+"F6.wireOp",EDGE,"E22");var subQ4=sQuery(id+"F6.wireOp",EDGE,"E21");var subQ5=sQuery(id+"F6.wireOp",EDGE,"E20");Q14=makeQuery(id+"F21.boolean.opBoolean","COPY",EDGE,{"derivedFrom":makeQuery(id+"F21.opLoft","MID_CAP_EDGE",EDGE,{"disambiguationData":[OSD([subQ5,subQ4,subQ3,subQ2,subQ0,subQ1]),TDD([makeQuery(id+"F18.imprint","INTERSECT",VERTEX,{"derivedFrom":[makeQuery(id+"F9.opLoft","MID_CAP_EDGE",EDGE,{"disambiguationData":[OSD([subQ5,subQ4,subQ3])],"capPos":0.0}),subQ2,subQ0]}),makeQuery(id+"F18.imprint","INTERSECT",VERTEX,{"derivedFrom":[subQ0,subQ1]}),makeQuery(id+"F18.imprint","IMPRINT",EDGE,{"derivedFrom":subQ0})])],"capPos":0.0})});}
            var Q15;
            {var subQ0=sQuery(id+"F18.wireOp",EDGE,"E51.2");var subQ1=sQuery(id+"F18.wireOp",EDGE,"E51.1");var subQ2=sQuery(id+"F6.wireOp",EDGE,"E22");var subQ3=sQuery(id+"F6.wireOp",EDGE,"E21");var subQ4=sQuery(id+"F6.wireOp",EDGE,"E20");var subQ5=sQuery(id+"F18.wireOp",EDGE,"E51.0");Q15=makeQuery(id+"F22.boolean.opBoolean","COPY",EDGE,{"derivedFrom":makeQuery(id+"F22.opLoft","MID_CAP_EDGE",EDGE,{"disambiguationData":[OSD([subQ4,subQ3,subQ2,subQ5,subQ1,subQ0]),TDD([makeQuery(id+"F18.imprint","INTERSECT",VERTEX,{"derivedFrom":[subQ5,subQ0]}),makeQuery(id+"F18.imprint","INTERSECT",VERTEX,{"derivedFrom":[makeQuery(id+"F9.opLoft","MID_CAP_EDGE",EDGE,{"disambiguationData":[OSD([subQ4,subQ3,subQ2])],"capPos":0.0}),subQ1,subQ0]}),makeQuery(id+"F18.imprint","IMPRINT",EDGE,{"derivedFrom":subQ0})])],"capPos":1.0})});}
            var Q16;
            {var subQ0=sQuery(id+"F19.wireOp",EDGE,"E61.2");var subQ1=sQuery(id+"F19.wireOp",EDGE,"E61.1");var subQ2=sQuery(id+"F8.wireOp",EDGE,"E28");var subQ3=sQuery(id+"F8.wireOp",EDGE,"E27");var subQ4=sQuery(id+"F8.wireOp",EDGE,"E24");var subQ5=sQuery(id+"F19.wireOp",EDGE,"E61.0");Q16=makeQuery(id+"F21.boolean.opBoolean","COPY",EDGE,{"derivedFrom":makeQuery(id+"F21.opLoft","MID_CAP_EDGE",EDGE,{"disambiguationData":[OSD([subQ4,subQ3,subQ2,subQ5,subQ1,subQ0]),TDD([makeQuery(id+"F19.imprint","INTERSECT",VERTEX,{"derivedFrom":[subQ5,subQ0]}),makeQuery(id+"F19.imprint","INTERSECT",VERTEX,{"derivedFrom":[makeQuery(id+"F9.opLoft","MID_CAP_EDGE",EDGE,{"disambiguationData":[OSD([subQ4,subQ3,subQ2])],"capPos":1.0}),subQ1,subQ0]}),makeQuery(id+"F19.imprint","IMPRINT",EDGE,{"derivedFrom":subQ0})])],"capPos":1.0})});}
            var Q17;
            {var subQ0=sQuery(id+"F19.wireOp",EDGE,"E63.1");var subQ1=sQuery(id+"F19.wireOp",EDGE,"E63.2");var subQ2=sQuery(id+"F19.wireOp",EDGE,"E63.0");var subQ3=sQuery(id+"F8.wireOp",EDGE,"E28");var subQ4=sQuery(id+"F8.wireOp",EDGE,"E27");var subQ5=sQuery(id+"F8.wireOp",EDGE,"E24");Q17=makeQuery(id+"F22.boolean.opBoolean","COPY",EDGE,{"derivedFrom":makeQuery(id+"F22.opLoft","MID_CAP_EDGE",EDGE,{"disambiguationData":[OSD([subQ5,subQ4,subQ3,subQ2,subQ0,subQ1]),TDD([makeQuery(id+"F19.imprint","INTERSECT",VERTEX,{"derivedFrom":[makeQuery(id+"F9.opLoft","MID_CAP_EDGE",EDGE,{"disambiguationData":[OSD([subQ5,subQ4,subQ3])],"capPos":1.0}),subQ2,subQ0]}),makeQuery(id+"F19.imprint","INTERSECT",VERTEX,{"derivedFrom":[subQ0,subQ1]}),makeQuery(id+"F19.imprint","IMPRINT",EDGE,{"derivedFrom":subQ0})])],"capPos":0.0})});}
            var Q18;
            Q18=makeQuery(id+"F25.opLoft","SWEPT_EDGE",EDGE,{"disambiguationData":[OSD([sQuery(id+"F14.wireOp",EDGE,"E30.bottom"),sQuery(id+"F14.wireOp",EDGE,"E30.left"),sQuery(id+"F15.wireOp",EDGE,"E40.top"),sQuery(id+"F15.wireOp",EDGE,"E40.left")])]});
            var Q19;
            Q19=makeQuery(id+"F25.opLoft","SWEPT_EDGE",EDGE,{"disambiguationData":[OSD([sQuery(id+"F14.wireOp",EDGE,"E30.bottom"),sQuery(id+"F14.wireOp",EDGE,"E30.right"),sQuery(id+"F15.wireOp",EDGE,"E40.top"),sQuery(id+"F15.wireOp",EDGE,"E40.right")])]});
            var Q20;
            Q20=makeQuery(id+"F25.opLoft","SWEPT_EDGE",EDGE,{"disambiguationData":[OSD([sQuery(id+"F14.wireOp",EDGE,"E30.top"),sQuery(id+"F14.wireOp",EDGE,"E30.left"),sQuery(id+"F15.wireOp",EDGE,"E40.bottom"),sQuery(id+"F15.wireOp",EDGE,"E40.left")])]});
            var Q21;
            Q21=makeQuery(id+"F25.opLoft","SWEPT_EDGE",EDGE,{"disambiguationData":[OSD([sQuery(id+"F14.wireOp",EDGE,"E30.top"),sQuery(id+"F14.wireOp",EDGE,"E30.right"),sQuery(id+"F15.wireOp",EDGE,"E40.bottom"),sQuery(id+"F15.wireOp",EDGE,"E40.right")])]});
            var Q22;
            Q22=makeQuery(id+"F26.opLoft","SWEPT_EDGE",EDGE,{"disambiguationData":[OSD([sQuery(id+"F14.wireOp",EDGE,"E31.bottom"),sQuery(id+"F14.wireOp",EDGE,"E31.right"),sQuery(id+"F15.wireOp",EDGE,"E41.top"),sQuery(id+"F15.wireOp",EDGE,"E41.right")])]});
            var Q23;
            Q23=makeQuery(id+"F26.opLoft","SWEPT_EDGE",EDGE,{"disambiguationData":[OSD([sQuery(id+"F14.wireOp",EDGE,"E31.top"),sQuery(id+"F14.wireOp",EDGE,"E31.right"),sQuery(id+"F15.wireOp",EDGE,"E41.bottom"),sQuery(id+"F15.wireOp",EDGE,"E41.right")])]});
            var Q24;
            Q24=makeQuery(id+"F26.opLoft","SWEPT_EDGE",EDGE,{"disambiguationData":[OSD([sQuery(id+"F14.wireOp",EDGE,"E31.bottom"),sQuery(id+"F14.wireOp",EDGE,"E31.left"),sQuery(id+"F15.wireOp",EDGE,"E41.top"),sQuery(id+"F15.wireOp",EDGE,"E41.left")])]});
            var Q25;
            Q25=makeQuery(id+"F26.opLoft","SWEPT_EDGE",EDGE,{"disambiguationData":[OSD([sQuery(id+"F14.wireOp",EDGE,"E31.top"),sQuery(id+"F14.wireOp",EDGE,"E31.left"),sQuery(id+"F15.wireOp",EDGE,"E41.bottom"),sQuery(id+"F15.wireOp",EDGE,"E41.left")])]});
            var Q26;
            Q26=makeQuery(id+"F24.opLoft","SWEPT_EDGE",EDGE,{"disambiguationData":[OSD([sQuery(id+"F14.wireOp",EDGE,"E33.bottom"),sQuery(id+"F14.wireOp",EDGE,"E33.right"),sQuery(id+"F15.wireOp",EDGE,"E42.top"),sQuery(id+"F15.wireOp",EDGE,"E42.right")])]});
            var Q27;
            Q27=makeQuery(id+"F24.opLoft","SWEPT_EDGE",EDGE,{"disambiguationData":[OSD([sQuery(id+"F14.wireOp",EDGE,"E33.bottom"),sQuery(id+"F14.wireOp",EDGE,"E33.left"),sQuery(id+"F15.wireOp",EDGE,"E42.top"),sQuery(id+"F15.wireOp",EDGE,"E42.left")])]});
            var Q28;
            Q28=makeQuery(id+"F23.opLoft","SWEPT_EDGE",EDGE,{"disambiguationData":[OSD([sQuery(id+"F14.wireOp",EDGE,"E32.bottom"),sQuery(id+"F14.wireOp",EDGE,"E32.right"),sQuery(id+"F15.wireOp",EDGE,"E43.top"),sQuery(id+"F15.wireOp",EDGE,"E43.right")])]});
            var Q29;
            Q29=makeQuery(id+"F23.opLoft","SWEPT_EDGE",EDGE,{"disambiguationData":[OSD([sQuery(id+"F14.wireOp",EDGE,"E32.bottom"),sQuery(id+"F14.wireOp",EDGE,"E32.left"),sQuery(id+"F15.wireOp",EDGE,"E43.top"),sQuery(id+"F15.wireOp",EDGE,"E43.left")])]});
            var Q30;
            Q30=makeQuery(id+"F23.opLoft","SWEPT_EDGE",EDGE,{"disambiguationData":[OSD([sQuery(id+"F14.wireOp",EDGE,"E32.top"),sQuery(id+"F14.wireOp",EDGE,"E32.right"),sQuery(id+"F15.wireOp",EDGE,"E43.bottom"),sQuery(id+"F15.wireOp",EDGE,"E43.right")])]});
            var Q31;
            Q31=makeQuery(id+"F23.opLoft","SWEPT_EDGE",EDGE,{"disambiguationData":[OSD([sQuery(id+"F14.wireOp",EDGE,"E32.top"),sQuery(id+"F14.wireOp",EDGE,"E32.left"),sQuery(id+"F15.wireOp",EDGE,"E43.bottom"),sQuery(id+"F15.wireOp",EDGE,"E43.left")])]});
            var Q32;
            Q32=makeQuery(id+"F24.opLoft","SWEPT_EDGE",EDGE,{"disambiguationData":[OSD([sQuery(id+"F14.wireOp",EDGE,"E33.top"),sQuery(id+"F14.wireOp",EDGE,"E33.right"),sQuery(id+"F15.wireOp",EDGE,"E42.bottom"),sQuery(id+"F15.wireOp",EDGE,"E42.right")])]});
            var Q33;
            Q33=makeQuery(id+"F24.opLoft","SWEPT_EDGE",EDGE,{"disambiguationData":[OSD([sQuery(id+"F14.wireOp",EDGE,"E33.top"),sQuery(id+"F14.wireOp",EDGE,"E33.left"),sQuery(id+"F15.wireOp",EDGE,"E42.bottom"),sQuery(id+"F15.wireOp",EDGE,"E42.left")])]});
            fillet(context, id + "F27", {"entities" : qUnion([Q0, Q1, Q2, Q3, Q4, Q5, Q6, Q7, Q8, Q9, Q10, Q11, Q12, Q13, Q14, Q15, Q16, Q17, Q18, Q19, Q20, Q21, Q22, Q23, Q24, Q25, Q26, Q27, Q28, Q29, Q30, Q31, Q32, Q33]), "radius" : 1 * mm, "tangentPropagation" : true, "allowEdgeOverflow" : false});
        }
        {
            var Q0;
            Q0=makeQuery(id+"F25.opLoft","MID_CAP_EDGE",EDGE,{"disambiguationData":[OSD([sQuery(id+"F15.wireOp",EDGE,"E40.top"),sQuery(id+"F15.wireOp",EDGE,"E40.left"),sQuery(id+"F15.wireOp",EDGE,"E40.right")])],"capPos":0.0});
            var Q1;
            Q1=makeQuery(id+"F25.opLoft","MID_CAP_EDGE",EDGE,{"disambiguationData":[OSD([sQuery(id+"F15.wireOp",EDGE,"E40.bottom"),sQuery(id+"F15.wireOp",EDGE,"E40.top"),sQuery(id+"F15.wireOp",EDGE,"E40.left")])],"capPos":0.0});
            var Q2;
            Q2=makeQuery(id+"F25.opLoft","MID_CAP_EDGE",EDGE,{"disambiguationData":[OSD([sQuery(id+"F15.wireOp",EDGE,"E40.bottom"),sQuery(id+"F15.wireOp",EDGE,"E40.left"),sQuery(id+"F15.wireOp",EDGE,"E40.right")])],"capPos":0.0});
            var Q3;
            Q3=makeQuery(id+"F25.opLoft","MID_CAP_EDGE",EDGE,{"disambiguationData":[OSD([sQuery(id+"F15.wireOp",EDGE,"E40.bottom"),sQuery(id+"F15.wireOp",EDGE,"E40.top"),sQuery(id+"F15.wireOp",EDGE,"E40.right")])],"capPos":0.0});
            var Q4;
            Q4=makeQuery(id+"F26.opLoft","MID_CAP_EDGE",EDGE,{"disambiguationData":[OSD([sQuery(id+"F15.wireOp",EDGE,"E41.bottom"),sQuery(id+"F15.wireOp",EDGE,"E41.top"),sQuery(id+"F15.wireOp",EDGE,"E41.right")])],"capPos":0.0});
            var Q5;
            Q5=makeQuery(id+"F26.opLoft","MID_CAP_EDGE",EDGE,{"disambiguationData":[OSD([sQuery(id+"F15.wireOp",EDGE,"E41.top"),sQuery(id+"F15.wireOp",EDGE,"E41.left"),sQuery(id+"F15.wireOp",EDGE,"E41.right")])],"capPos":0.0});
            var Q6;
            Q6=makeQuery(id+"F26.opLoft","MID_CAP_EDGE",EDGE,{"disambiguationData":[OSD([sQuery(id+"F15.wireOp",EDGE,"E41.bottom"),sQuery(id+"F15.wireOp",EDGE,"E41.top"),sQuery(id+"F15.wireOp",EDGE,"E41.left")])],"capPos":0.0});
            var Q7;
            Q7=makeQuery(id+"F26.opLoft","MID_CAP_EDGE",EDGE,{"disambiguationData":[OSD([sQuery(id+"F15.wireOp",EDGE,"E41.bottom"),sQuery(id+"F15.wireOp",EDGE,"E41.left"),sQuery(id+"F15.wireOp",EDGE,"E41.right")])],"capPos":0.0});
            var Q8;
            Q8=makeQuery(id+"F26.opLoft","MID_CAP_EDGE",EDGE,{"disambiguationData":[OSD([sQuery(id+"F14.wireOp",EDGE,"E31.bottom"),sQuery(id+"F14.wireOp",EDGE,"E31.left"),sQuery(id+"F14.wireOp",EDGE,"E31.right")])],"capPos":1.0});
            var Q9;
            Q9=makeQuery(id+"F26.opLoft","MID_CAP_EDGE",EDGE,{"disambiguationData":[OSD([sQuery(id+"F14.wireOp",EDGE,"E31.bottom"),sQuery(id+"F14.wireOp",EDGE,"E31.top"),sQuery(id+"F14.wireOp",EDGE,"E31.left")])],"capPos":1.0});
            var Q10;
            Q10=makeQuery(id+"F26.opLoft","MID_CAP_EDGE",EDGE,{"disambiguationData":[OSD([sQuery(id+"F14.wireOp",EDGE,"E31.top"),sQuery(id+"F14.wireOp",EDGE,"E31.left"),sQuery(id+"F14.wireOp",EDGE,"E31.right")])],"capPos":1.0});
            var Q11;
            Q11=makeQuery(id+"F26.opLoft","MID_CAP_EDGE",EDGE,{"disambiguationData":[OSD([sQuery(id+"F14.wireOp",EDGE,"E31.bottom"),sQuery(id+"F14.wireOp",EDGE,"E31.top"),sQuery(id+"F14.wireOp",EDGE,"E31.right")])],"capPos":1.0});
            var Q12;
            Q12=makeQuery(id+"F25.opLoft","MID_CAP_EDGE",EDGE,{"disambiguationData":[OSD([sQuery(id+"F14.wireOp",EDGE,"E30.bottom"),sQuery(id+"F14.wireOp",EDGE,"E30.top"),sQuery(id+"F14.wireOp",EDGE,"E30.left")])],"capPos":1.0});
            var Q13;
            Q13=makeQuery(id+"F25.opLoft","MID_CAP_EDGE",EDGE,{"disambiguationData":[OSD([sQuery(id+"F14.wireOp",EDGE,"E30.bottom"),sQuery(id+"F14.wireOp",EDGE,"E30.left"),sQuery(id+"F14.wireOp",EDGE,"E30.right")])],"capPos":1.0});
            var Q14;
            Q14=makeQuery(id+"F25.opLoft","MID_CAP_EDGE",EDGE,{"disambiguationData":[OSD([sQuery(id+"F14.wireOp",EDGE,"E30.bottom"),sQuery(id+"F14.wireOp",EDGE,"E30.top"),sQuery(id+"F14.wireOp",EDGE,"E30.right")])],"capPos":1.0});
            var Q15;
            Q15=makeQuery(id+"F25.opLoft","MID_CAP_EDGE",EDGE,{"disambiguationData":[OSD([sQuery(id+"F14.wireOp",EDGE,"E30.top"),sQuery(id+"F14.wireOp",EDGE,"E30.left"),sQuery(id+"F14.wireOp",EDGE,"E30.right")])],"capPos":1.0});
            var Q16;
            Q16=makeQuery(id+"F24.opLoft","MID_CAP_EDGE",EDGE,{"disambiguationData":[OSD([sQuery(id+"F15.wireOp",EDGE,"E42.bottom"),sQuery(id+"F15.wireOp",EDGE,"E42.left"),sQuery(id+"F15.wireOp",EDGE,"E42.right")])],"capPos":0.0});
            var Q17;
            Q17=makeQuery(id+"F23.opLoft","MID_CAP_EDGE",EDGE,{"disambiguationData":[OSD([sQuery(id+"F15.wireOp",EDGE,"E43.bottom"),sQuery(id+"F15.wireOp",EDGE,"E43.left"),sQuery(id+"F15.wireOp",EDGE,"E43.right")])],"capPos":0.0});
            var Q18;
            Q18=makeQuery(id+"F24.opLoft","MID_CAP_EDGE",EDGE,{"disambiguationData":[OSD([sQuery(id+"F14.wireOp",EDGE,"E33.top"),sQuery(id+"F14.wireOp",EDGE,"E33.left"),sQuery(id+"F14.wireOp",EDGE,"E33.right")])],"capPos":1.0});
            var Q19;
            Q19=makeQuery(id+"F23.opLoft","MID_CAP_EDGE",EDGE,{"disambiguationData":[OSD([sQuery(id+"F14.wireOp",EDGE,"E32.top"),sQuery(id+"F14.wireOp",EDGE,"E32.left"),sQuery(id+"F14.wireOp",EDGE,"E32.right")])],"capPos":1.0});
            var Q20;
            Q20=makeQuery(id+"F16.opExtrude","CAP_EDGE",EDGE,{"disambiguationData":[OSD([sQuery(id+"F15.wireOp",EDGE,"E34.0")])],"isStart":true});
            var Q21;
            Q21=makeQuery(id+"F16.opExtrude","CAP_EDGE",EDGE,{"disambiguationData":[OSD([sQuery(id+"F15.wireOp",EDGE,"E39.0")])],"isStart":true});
            var Q22;
            Q22=makeQuery(id+"F16.opExtrude","CAP_EDGE",EDGE,{"disambiguationData":[OSD([sQuery(id+"F15.wireOp",EDGE,"E38.0")])],"isStart":true});
            var Q23;
            Q23=makeQuery(id+"F9.opLoft","MID_CAP_EDGE",EDGE,{"disambiguationData":[OSD([sQuery(id+"F8.wireOp",EDGE,"E23"),sQuery(id+"F8.wireOp",EDGE,"E27"),sQuery(id+"F8.wireOp",EDGE,"E28")])],"capPos":1.0});
            var Q24;
            Q24=makeQuery(id+"F9.opLoft","MID_CAP_EDGE",EDGE,{"disambiguationData":[OSD([sQuery(id+"F6.wireOp",EDGE,"E19"),sQuery(id+"F6.wireOp",EDGE,"E20"),sQuery(id+"F6.wireOp",EDGE,"E22")])],"capPos":0.0});
            var Q25;
            {var subQ3=sQuery(id+"F8.wireOp",EDGE,"E27");var subQ4=sQuery(id+"F8.wireOp",EDGE,"E24");var subQ10=sQuery(id+"F6.wireOp",EDGE,"E22");var subQ11=sQuery(id+"F6.wireOp",EDGE,"E21");var subQ12=sQuery(id+"F6.wireOp",EDGE,"E20");var subQ13=makeQuery(id+"F9.opLoft","MID_CAP_EDGE",EDGE,{"disambiguationData":[OSD([subQ12,subQ11,subQ10])],"capPos":0.0});var subQ16=sQuery(id+"F6.wireOp",EDGE,"E19");Q25=makeQuery(id+"F21.boolean.opBoolean","SPLIT",EDGE,{"disambiguationData":[TD([makeQuery(id+"F9.opLoft","SWEPT_FACE",FACE,{"disambiguationData":[OSD([subQ16,subQ11,subQ10,sQuery(id+"F8.wireOp",EDGE,"E23"),subQ4,subQ3])]})])],"derivedFrom":subQ13});}
            var Q26;
            {var subQ0=sQuery(id+"F19.wireOp",EDGE,"E61.1");var subQ1=sQuery(id+"F19.wireOp",EDGE,"E61.2");var subQ2=sQuery(id+"F8.wireOp",EDGE,"E28");var subQ3=sQuery(id+"F8.wireOp",EDGE,"E27");var subQ4=sQuery(id+"F8.wireOp",EDGE,"E24");var subQ5=makeQuery(id+"F9.opLoft","MID_CAP_EDGE",EDGE,{"disambiguationData":[OSD([subQ4,subQ3,subQ2])],"capPos":1.0});var subQ6=makeQuery(id+"F19.imprint","INTERSECT",VERTEX,{"derivedFrom":[subQ5,subQ0,subQ1]});var subQ7=sQuery(id+"F19.wireOp",EDGE,"E61.0");var subQ8=sQuery(id+"F18.wireOp",EDGE,"E53.0");var subQ9=sQuery(id+"F18.wireOp",EDGE,"E53.2");var subQ10=sQuery(id+"F6.wireOp",EDGE,"E22");var subQ11=sQuery(id+"F6.wireOp",EDGE,"E21");var subQ12=sQuery(id+"F6.wireOp",EDGE,"E20");var subQ13=makeQuery(id+"F9.opLoft","MID_CAP_EDGE",EDGE,{"disambiguationData":[OSD([subQ12,subQ11,subQ10])],"capPos":0.0});var subQ14=sQuery(id+"F18.wireOp",EDGE,"E53.1");var subQ15=makeQuery(id+"F18.imprint","INTERSECT",VERTEX,{"derivedFrom":[subQ13,subQ8,subQ14]});var subQ17=sQuery(id+"F6.wireOp",EDGE,"E19");var subQ19=makeQuery(id+"F21.opLoft","SWEPT_FACE",FACE,{"disambiguationData":[OSD([subQ12,subQ11,subQ10,subQ4,subQ3,subQ2,subQ8,subQ14,subQ9,subQ7,subQ0,subQ1]),TDD([subQ15,makeQuery(id+"F18.imprint","INTERSECT",VERTEX,{"derivedFrom":[subQ14,subQ9]}),makeQuery(id+"F18.imprint","IMPRINT",EDGE,{"derivedFrom":subQ14}),makeQuery(id+"F19.imprint","INTERSECT",VERTEX,{"derivedFrom":[subQ7,subQ1]}),subQ6,makeQuery(id+"F19.imprint","IMPRINT",EDGE,{"derivedFrom":subQ1})])]});Q26=makeQuery(id+"F22.boolean.opBoolean","SPLIT",EDGE,{"disambiguationData":[TD([makeQuery(id+"F21.boolean.opBoolean","COPY",FACE,{"derivedFrom":subQ19})])],"derivedFrom":makeQuery(id+"F21.boolean.opBoolean","SPLIT",EDGE,{"disambiguationData":[TD([makeQuery(id+"F9.opLoft","SWEPT_FACE",FACE,{"disambiguationData":[OSD([subQ17,subQ12,subQ11,sQuery(id+"F8.wireOp",EDGE,"E23"),subQ4,subQ2])]})])],"derivedFrom":subQ13})});}
            var Q27;
            {var subQ2=sQuery(id+"F8.wireOp",EDGE,"E28");var subQ4=sQuery(id+"F8.wireOp",EDGE,"E24");var subQ10=sQuery(id+"F6.wireOp",EDGE,"E22");var subQ11=sQuery(id+"F6.wireOp",EDGE,"E21");var subQ12=sQuery(id+"F6.wireOp",EDGE,"E20");var subQ13=makeQuery(id+"F9.opLoft","MID_CAP_EDGE",EDGE,{"disambiguationData":[OSD([subQ12,subQ11,subQ10])],"capPos":0.0});var subQ17=sQuery(id+"F6.wireOp",EDGE,"E19");var subQ19=makeQuery(id+"F9.opLoft","SWEPT_FACE",FACE,{"disambiguationData":[OSD([subQ17,subQ12,subQ11,sQuery(id+"F8.wireOp",EDGE,"E23"),subQ4,subQ2])]});Q27=makeQuery(id+"F22.boolean.opBoolean","SPLIT",EDGE,{"disambiguationData":[TD([subQ19])],"derivedFrom":makeQuery(id+"F21.boolean.opBoolean","SPLIT",EDGE,{"disambiguationData":[TD([subQ19])],"derivedFrom":subQ13})});}
            fillet(context, id + "F28", {"entities" : qUnion([Q0, Q1, Q2, Q3, Q4, Q5, Q6, Q7, Q8, Q9, Q10, Q11, Q12, Q13, Q14, Q15, Q16, Q17, Q18, Q19, Q20, Q21, Q22, Q23, Q24, Q25, Q26, Q27]), "radius" : 3 * mm, "tangentPropagation" : true, "allowEdgeOverflow" : false});
        }
    });
